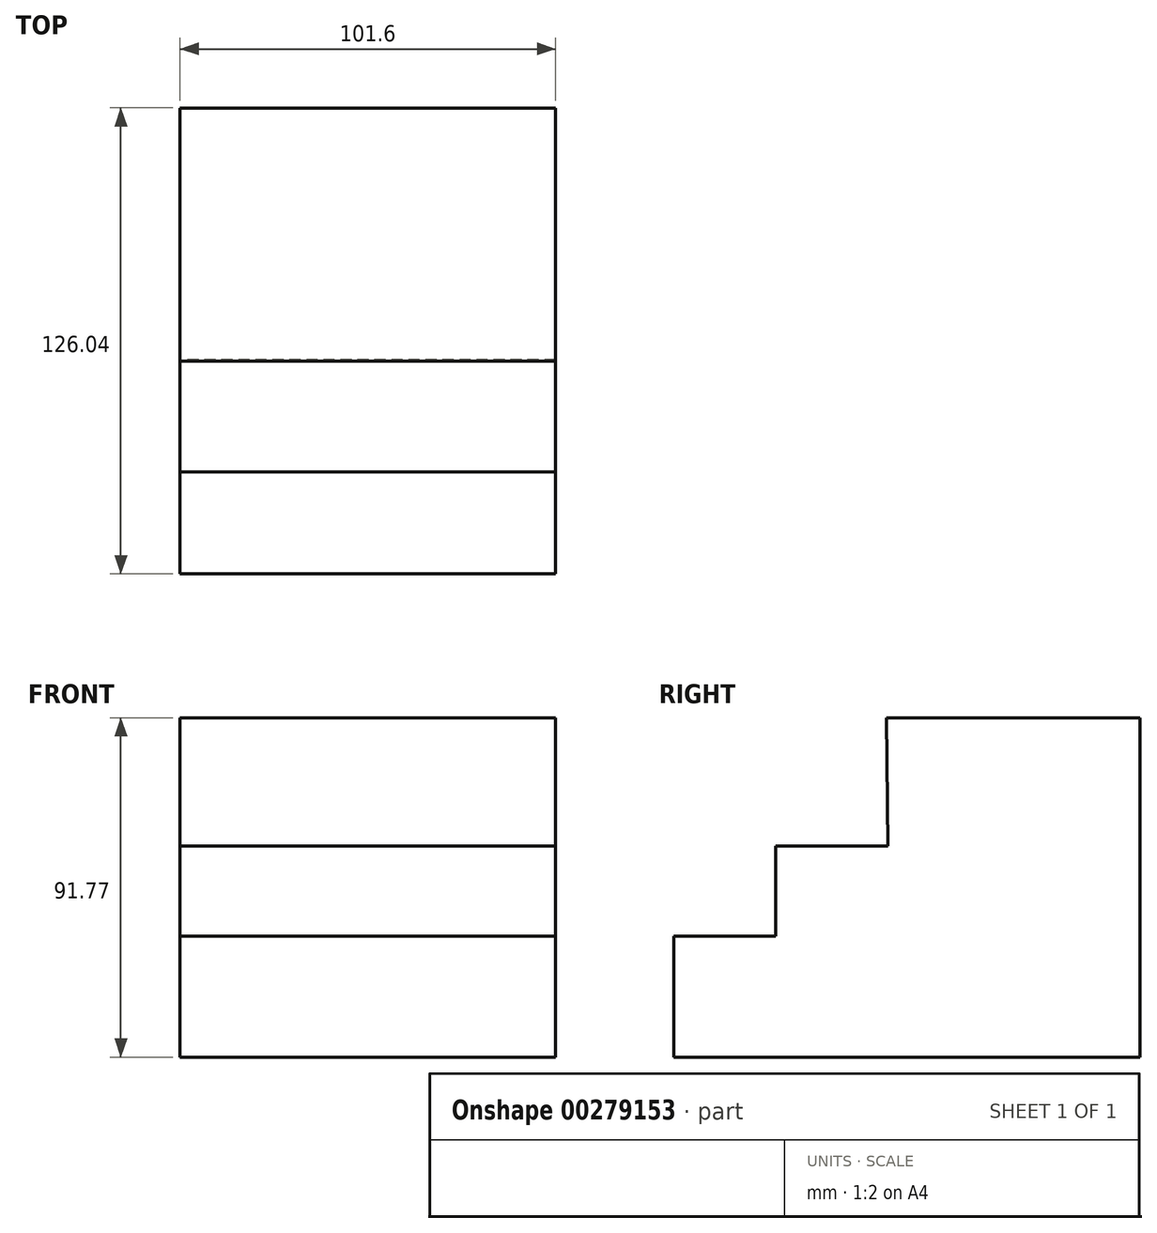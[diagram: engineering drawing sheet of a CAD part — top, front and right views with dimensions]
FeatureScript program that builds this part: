
annotation { "Feature Type Name" : "Feature", "Feature Type Description" : "" }
export const myFeature = defineFeature(function(context is Context, id is Id, definition is map)
    precondition{}
    {
        {
            var Q0;
            Q0=qCreatedBy(makeId("Right.planeOp"),FACE);
            var sketch = newSketch(context, id + "F0", { "sketchPlane" : qUnion([Q0])});
            skLineSegment(sketch, "E0", {"start": v(-18.9, 69.02) * mm, "end": v(49.63, 69.02) * mm});
            skLineSegment(sketch, "E1", {"start": v(49.63, 69.02) * mm, "end": v(49.63, -22.75) * mm});
            skLineSegment(sketch, "E2", {"start": v(49.63, -22.75) * mm, "end": v(-76.4, -22.75) * mm});
            skLineSegment(sketch, "E3", {"start": v(-76.4, -22.75) * mm, "end": v(-76.4, 9.94) * mm});
            skLineSegment(sketch, "E4", {"start": v(-76.4, 9.94) * mm, "end": v(-48.84, 9.94) * mm});
            skLineSegment(sketch, "E5", {"start": v(-48.84, 9.94) * mm, "end": v(-48.84, 34.36) * mm});
            skLineSegment(sketch, "E6", {"start": v(-48.84, 34.36) * mm, "end": v(-18.51, 34.36) * mm});
            skLineSegment(sketch, "E7", {"start": v(-18.51, 34.36) * mm, "end": v(-18.9, 69.02) * mm});
            skSolve(sketch);
        }
        {
            var Q0;
            Q0 = qSketchRegion(id + "F0", true);
            extrude(context, id + "F1", {"entities" : qUnion([Q0]), "depth" : 101.6 * mm});
        }
    });
